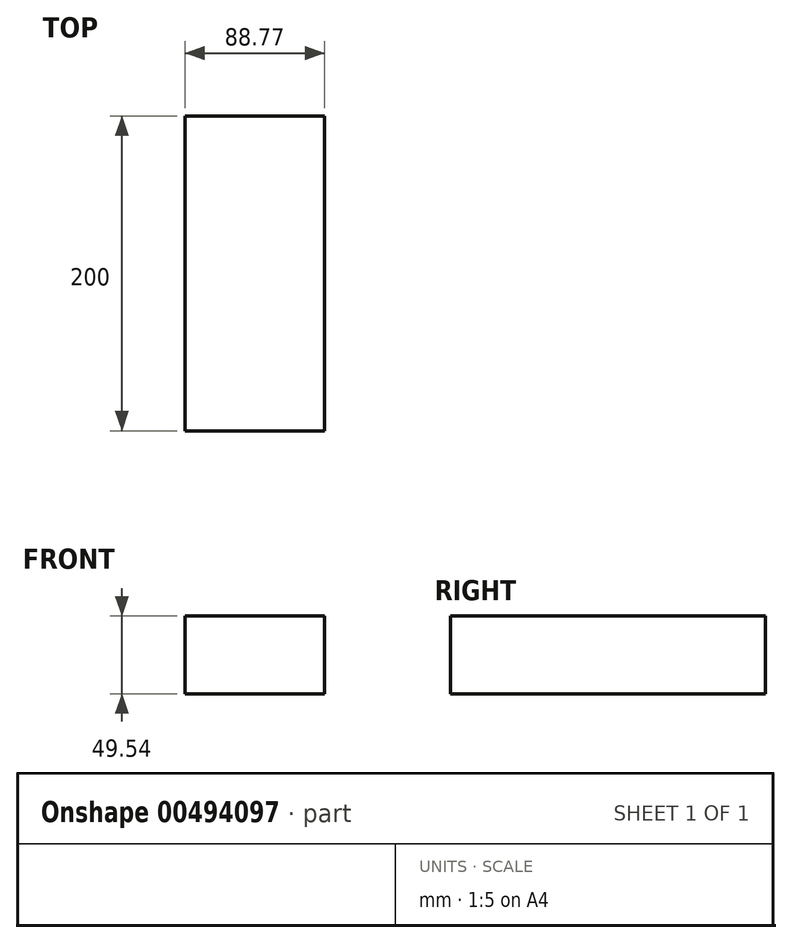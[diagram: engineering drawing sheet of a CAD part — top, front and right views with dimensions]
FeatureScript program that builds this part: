
annotation { "Feature Type Name" : "Feature", "Feature Type Description" : "" }
export const myFeature = defineFeature(function(context is Context, id is Id, definition is map)
    precondition{}
    {
        {
            var Q0;
            Q0=qCreatedBy(makeId("Front.planeOp"),FACE);
            var sketch = newSketch(context, id + "F0", { "sketchPlane" : qUnion([Q0])});
            skLineSegment(sketch, "E0.bottom", {"start": v(-38.56, 15.9) * mm, "end": v(50.21, 15.9) * mm});
            skLineSegment(sketch, "E0.top", {"start": v(-38.56, -33.65) * mm, "end": v(50.21, -33.65) * mm});
            skLineSegment(sketch, "E0.left", {"start": v(-38.56, 15.9) * mm, "end": v(-38.56, -33.65) * mm});
            skLineSegment(sketch, "E0.right", {"start": v(50.21, 15.9) * mm, "end": v(50.21, -33.65) * mm});
            skSolve(sketch);
        }
        {
            var Q0;
            Q0=makeQuery(id+"F0.imprint","IMPRINT",FACE,{"disambiguationData":[TD([[makeQuery(id+"F0.imprint","IMPRINT",EDGE,{"derivedFrom":sQuery(id+"F0.wireOp",EDGE,"E0.bottom")}),-1.0]])]});
            extrude(context, id + "F1", {"entities" : qUnion([Q0]), "depth" : 200 * mm});
        }
    });
